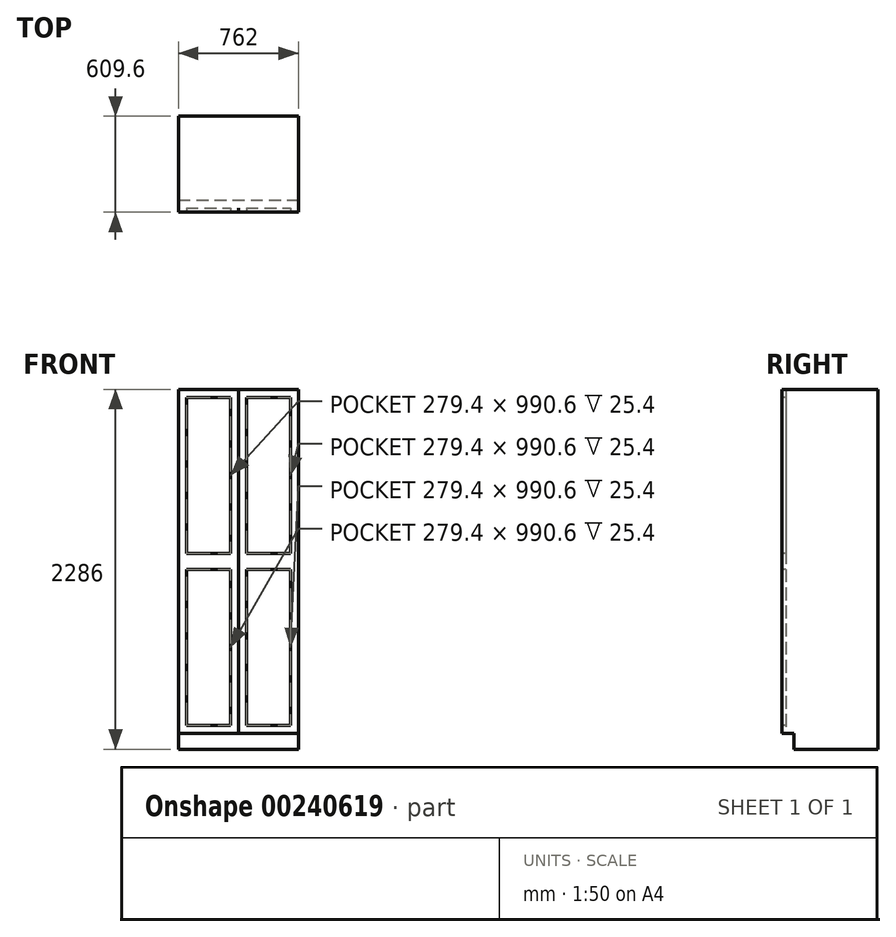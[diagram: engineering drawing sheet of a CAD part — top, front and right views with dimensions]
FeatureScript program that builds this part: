
annotation { "Feature Type Name" : "Feature", "Feature Type Description" : "" }
export const myFeature = defineFeature(function(context is Context, id is Id, definition is map)
    precondition{}
    {
        {
            var Q0;
            Q0=qCreatedBy(makeId("Top.planeOp"),FACE);
            var sketch = newSketch(context, id + "F0", { "sketchPlane" : qUnion([Q0])});
            skLineSegment(sketch, "E0.bottom", {"start": v(-304.8, 304.8) * mm, "end": v(457.2, 304.8) * mm});
            skLineSegment(sketch, "E0.top", {"start": v(-304.8, -304.8) * mm, "end": v(457.2, -304.8) * mm});
            skLineSegment(sketch, "E0.left", {"start": v(-304.8, 304.8) * mm, "end": v(-304.8, -304.8) * mm});
            skLineSegment(sketch, "E0.right", {"start": v(457.2, 304.8) * mm, "end": v(457.2, -304.8) * mm});
            skSolve(sketch);
        }
        {
            var Q0;
            Q0=makeQuery(id+"F0.imprint","IMPRINT",FACE,{"disambiguationData":[TD([[makeQuery(id+"F0.imprint","IMPRINT",EDGE,{"derivedFrom":sQuery(id+"F0.wireOp",EDGE,"E0.bottom")}),-1.0]])]});
            extrude(context, id + "F1", {"entities" : qUnion([Q0]), "depth" : 2286 * mm, "offsetDistance" : 25.4 * mm});
        }
        {
            var Q0;
            Q0=makeQuery(id+"F1.opExtrude","SWEPT_FACE",FACE,{"disambiguationData":[OSD([sQuery(id+"F0.wireOp",EDGE,"E0.top")])]});
            var sketch = newSketch(context, id + "F2", { "sketchPlane" : qUnion([Q0])});
            skLineSegment(sketch, "E1.bottom", {"start": v(-304.8, 0) * mm, "end": v(457.2, 0) * mm});
            skLineSegment(sketch, "E1.top", {"start": v(-304.8, 101.6) * mm, "end": v(457.2, 101.6) * mm});
            skLineSegment(sketch, "E1.left", {"start": v(-304.8, 0) * mm, "end": v(-304.8, 101.6) * mm});
            skLineSegment(sketch, "E1.right", {"start": v(457.2, 0) * mm, "end": v(457.2, 101.6) * mm});
            skSolve(sketch);
        }
        {
            var Q0;
            Q0=makeQuery(id+"F2.imprint","IMPRINT",FACE,{"disambiguationData":[TD([[makeQuery(id+"F2.imprint","IMPRINT",EDGE,{"derivedFrom":sQuery(id+"F2.wireOp",EDGE,"E1.bottom")}),1.0]])]});
            extrude(context, id + "F3", {"entities" : qUnion([Q0]), "operationType" : NewBodyOperationType.REMOVE, "oppositeDirection" : true, "depth" : 76.2 * mm, "offsetDistance" : 25.4 * mm});
        }
        {
            var Q0;
            Q0=makeQuery(id+"F1.opExtrude","SWEPT_FACE",FACE,{"disambiguationData":[OSD([sQuery(id+"F0.wireOp",EDGE,"E0.top")])]});
            var sketch = newSketch(context, id + "F4", { "sketchPlane" : qUnion([Q0])});
            skLineSegment(sketch, "E2.bottom", {"start": v(-254, 2235.2) * mm, "end": v(25.4, 2235.2) * mm});
            skLineSegment(sketch, "E2.top", {"start": v(-254, 1244.6) * mm, "end": v(25.4, 1244.6) * mm});
            skLineSegment(sketch, "E2.left", {"start": v(-254, 2235.2) * mm, "end": v(-254, 1244.6) * mm});
            skLineSegment(sketch, "E2.right", {"start": v(25.4, 2235.2) * mm, "end": v(25.4, 1244.6) * mm});
            skLineSegment(sketch, "E3.bottom", {"start": v(-254, 1143) * mm, "end": v(25.4, 1143) * mm});
            skLineSegment(sketch, "E3.top", {"start": v(-254, 152.4) * mm, "end": v(25.4, 152.4) * mm});
            skLineSegment(sketch, "E3.left", {"start": v(-254, 1143) * mm, "end": v(-254, 152.4) * mm});
            skLineSegment(sketch, "E3.right", {"start": v(25.4, 1143) * mm, "end": v(25.4, 152.4) * mm});
            skLineSegment(sketch, "E4.bottom", {"start": v(127, 2235.2) * mm, "end": v(406.4, 2235.2) * mm});
            skLineSegment(sketch, "E4.top", {"start": v(127, 1244.6) * mm, "end": v(406.4, 1244.6) * mm});
            skLineSegment(sketch, "E4.left", {"start": v(127, 2235.2) * mm, "end": v(127, 1244.6) * mm});
            skLineSegment(sketch, "E4.right", {"start": v(406.4, 2235.2) * mm, "end": v(406.4, 1244.6) * mm});
            skLineSegment(sketch, "E5.bottom", {"start": v(127, 1143) * mm, "end": v(406.4, 1143) * mm});
            skLineSegment(sketch, "E5.top", {"start": v(127, 152.4) * mm, "end": v(406.4, 152.4) * mm});
            skLineSegment(sketch, "E5.left", {"start": v(127, 1143) * mm, "end": v(127, 152.4) * mm});
            skLineSegment(sketch, "E5.right", {"start": v(406.4, 1143) * mm, "end": v(406.4, 152.4) * mm});
            skLineSegment(sketch, "E6.bottom", {"start": v(75.57, 2286) * mm, "end": v(76.84, 2286) * mm});
            skLineSegment(sketch, "E6.top", {"start": v(75.57, 101.6) * mm, "end": v(76.84, 101.6) * mm});
            skLineSegment(sketch, "E6.left", {"start": v(75.57, 2286) * mm, "end": v(75.57, 101.6) * mm});
            skLineSegment(sketch, "E6.right", {"start": v(76.84, 2286) * mm, "end": v(76.84, 101.6) * mm});
            skSolve(sketch);
        }
        {
            var Q0;
            Q0=makeQuery(id+"F4.imprint","IMPRINT",FACE,{"disambiguationData":[TD([[makeQuery(id+"F4.imprint","IMPRINT",EDGE,{"derivedFrom":sQuery(id+"F4.wireOp",EDGE,"E2.bottom")}),-1.0]])]});
            var Q1;
            Q1=makeQuery(id+"F4.imprint","IMPRINT",FACE,{"disambiguationData":[TD([[makeQuery(id+"F4.imprint","IMPRINT",EDGE,{"derivedFrom":sQuery(id+"F4.wireOp",EDGE,"E4.bottom")}),-1.0]])]});
            var Q2;
            Q2=makeQuery(id+"F4.imprint","IMPRINT",FACE,{"disambiguationData":[TD([[makeQuery(id+"F4.imprint","IMPRINT",EDGE,{"derivedFrom":sQuery(id+"F4.wireOp",EDGE,"E5.bottom")}),-1.0]])]});
            var Q3;
            Q3=makeQuery(id+"F4.imprint","IMPRINT",FACE,{"disambiguationData":[TD([[makeQuery(id+"F4.imprint","IMPRINT",EDGE,{"derivedFrom":sQuery(id+"F4.wireOp",EDGE,"E3.bottom")}),-1.0]])]});
            var Q4;
            Q4=makeQuery(id+"F4.imprint","IMPRINT",FACE,{"disambiguationData":[TD([[makeQuery(id+"F4.imprint","IMPRINT",EDGE,{"derivedFrom":sQuery(id+"F4.wireOp",EDGE,"E6.bottom")}),-1.0]])]});
            extrude(context, id + "F5", {"entities" : qUnion([Q0, Q1, Q2, Q3, Q4]), "operationType" : NewBodyOperationType.REMOVE, "oppositeDirection" : true, "depth" : 25.4 * mm, "offsetDistance" : 25.4 * mm});
        }
    });
